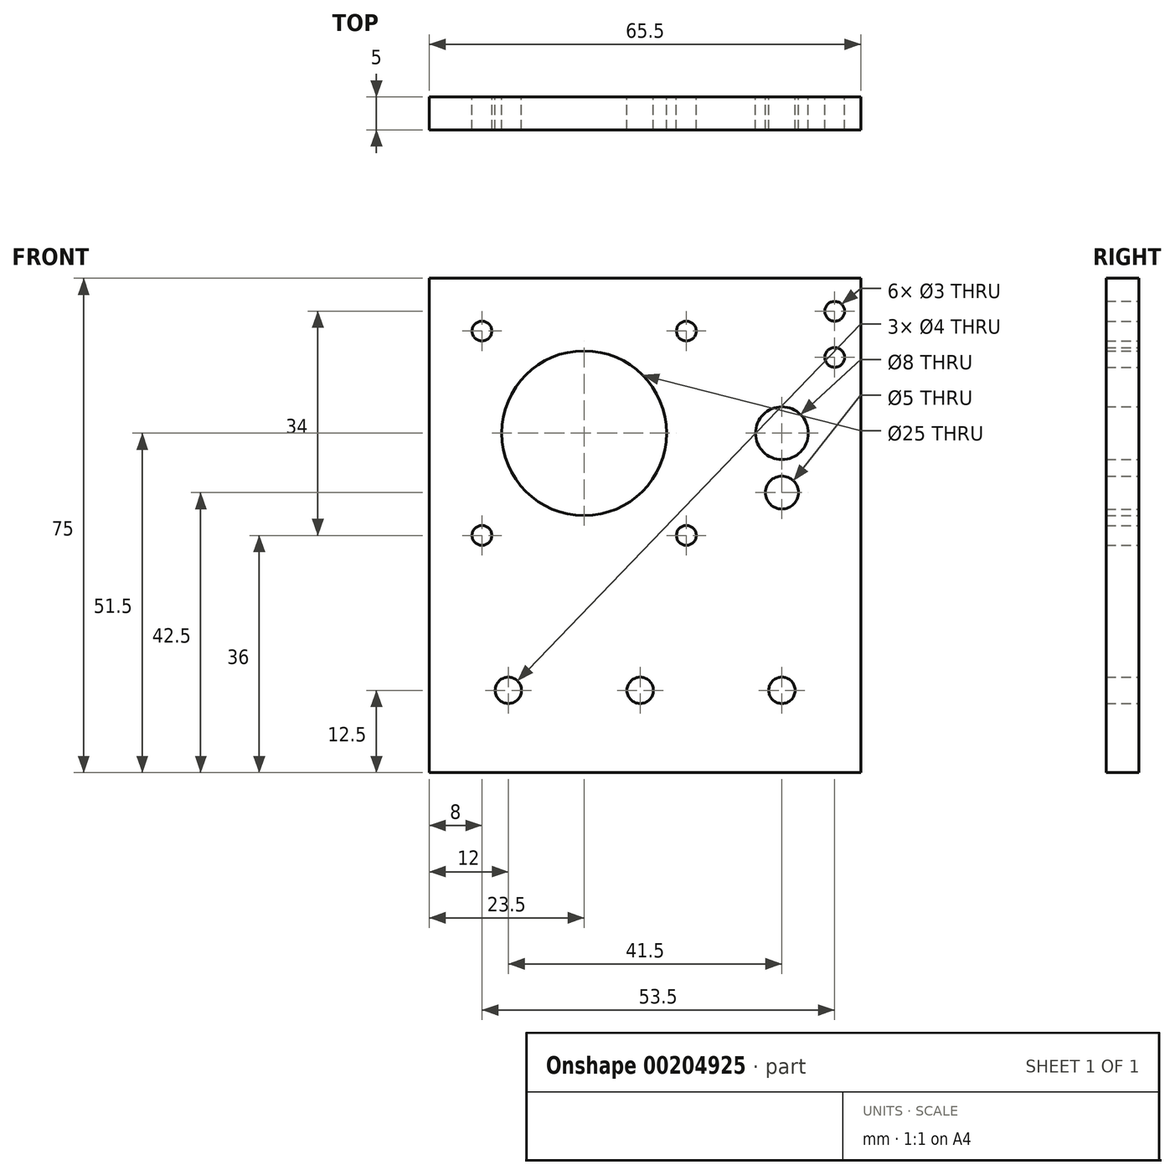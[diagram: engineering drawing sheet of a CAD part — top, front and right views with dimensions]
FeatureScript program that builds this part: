
annotation { "Feature Type Name" : "Feature", "Feature Type Description" : "" }
export const myFeature = defineFeature(function(context is Context, id is Id, definition is map)
    precondition{}
    {
        {
            var Q0;
            Q0=qCreatedBy(makeId("Front.planeOp"),FACE);
            var sketch = newSketch(context, id + "F0", { "sketchPlane" : qUnion([Q0])});
            skLineSegment(sketch, "E0.bottom", {"start": v(0, 0) * mm, "end": v(47, 0) * mm});
            skLineSegment(sketch, "E0.top", {"start": v(0, 50) * mm, "end": v(47, 50) * mm});
            skLineSegment(sketch, "E0.left", {"start": v(0, 0) * mm, "end": v(0, 50) * mm});
            skLineSegment(sketch, "E0.right", {"start": v(47, 0) * mm, "end": v(47, 50) * mm});
            skLineSegment(sketch, "E1.bottom", {"start": v(8, 11) * mm, "end": v(39, 11) * mm, "construction": true});
            skLineSegment(sketch, "E1.top", {"start": v(8, 42) * mm, "end": v(39, 42) * mm, "construction": true});
            skLineSegment(sketch, "E1.left", {"start": v(8, 11) * mm, "end": v(8, 42) * mm, "construction": true});
            skLineSegment(sketch, "E1.right", {"start": v(39, 11) * mm, "end": v(39, 42) * mm, "construction": true});
            skCircle(sketch, "E2", {"center": v(8, 42) * mm, "radius": 1.5 * mm});
            skCircle(sketch, "E3", {"center": v(39, 42) * mm, "radius": 1.5 * mm});
            skCircle(sketch, "E4", {"center": v(39, 11) * mm, "radius": 1.5 * mm});
            skCircle(sketch, "E5", {"center": v(8, 11) * mm, "radius": 1.5 * mm});
            skLineSegment(sketch, "E6", {"start": v(8, 11) * mm, "end": v(39, 42) * mm});
            skPoint(sketch, "E7", {"position": v(23.5, 26.5) * mm});
            skLineSegment(sketch, "E8", {"start": v(23.5, 26.5) * mm, "end": v(53.5, 26.5) * mm, "construction": true});
            skCircle(sketch, "E9", {"center": v(53.5, 26.5) * mm, "radius": 4 * mm});
            skCircle(sketch, "E10", {"center": v(53.5, 26.5) * mm, "radius": 12 * mm, "construction": true});
            skLineSegment(sketch, "E11.top", {"start": v(0, -25) * mm, "end": v(47, -25) * mm});
            skLineSegment(sketch, "E11.left", {"start": v(0, 0) * mm, "end": v(0, -25) * mm});
            skLineSegment(sketch, "E11.right", {"start": v(47, 0) * mm, "end": v(47, -25) * mm});
            skCircle(sketch, "E12", {"center": v(23.5, 26.5) * mm, "radius": 12.5 * mm});
            skLineSegment(sketch, "E13", {"start": v(53.5, 26.5) * mm, "end": v(53.5, 17.5) * mm});
            skCircle(sketch, "E14", {"center": v(53.5, 17.5) * mm, "radius": 2.5 * mm});
            skLineSegment(sketch, "E15", {"start": v(53.5, 26.5) * mm, "end": v(65.5, 26.5) * mm, "construction": true});
            skLineSegment(sketch, "E16", {"start": v(65.5, 26.5) * mm, "end": v(65.5, -25) * mm});
            skLineSegment(sketch, "E17", {"start": v(65.5, -25) * mm, "end": v(47, -25) * mm});
            skLineSegment(sketch, "E18", {"start": v(65.5, 26.5) * mm, "end": v(65.5, 50) * mm});
            skLineSegment(sketch, "E19", {"start": v(65.5, 50) * mm, "end": v(47, 50) * mm});
            skLineSegment(sketch, "E20", {"start": v(47, -12.5) * mm, "end": v(0, -12.5) * mm});
            skLineSegment(sketch, "E21", {"start": v(47, -12.5) * mm, "end": v(65.5, -12.5) * mm});
            skCircle(sketch, "E22", {"center": v(12, -12.5) * mm, "radius": 2 * mm});
            skCircle(sketch, "E23", {"center": v(32, -12.5) * mm, "radius": 2 * mm});
            skCircle(sketch, "E24", {"center": v(53.5, -12.5) * mm, "radius": 2 * mm});
            skLineSegment(sketch, "E25", {"start": v(61.5, 50) * mm, "end": v(61.5, 45) * mm});
            skLineSegment(sketch, "E26", {"start": v(61.5, 45) * mm, "end": v(61.5, 38) * mm});
            skCircle(sketch, "E27", {"center": v(61.5, 45) * mm, "radius": 1.5 * mm});
            skCircle(sketch, "E28", {"center": v(61.5, 38) * mm, "radius": 1.5 * mm});
            skSolve(sketch);
        }
        {
            var Q0;
            {var subQ0=sQuery(id+"F0.wireOp",EDGE,"E0.top");Q0=makeQuery(id+"F0.imprint","IMPRINT",FACE,{"disambiguationData":[TD([[makeQuery(id+"F0.imprint","IMPRINT",EDGE,{"derivedFrom":subQ0}),-1.0]])]});}
            var Q1;
            {var subQ0=sQuery(id+"F0.wireOp",EDGE,"E8");var subQ1=sQuery(id+"F0.wireOp",EDGE,"E0.right");var subQ2=makeQuery(id+"F0.imprint","INTERSECT",VERTEX,{"derivedFrom":[subQ1,subQ0]});Q1=makeQuery(id+"F0.imprint","IMPRINT",FACE,{"disambiguationData":[TD([[makeQuery(id+"F0.imprint","IMPRINT",EDGE,{"disambiguationData":[TD([[subQ2,1.0]])],"derivedFrom":subQ1}),1.0]])]});}
            var Q2;
            {var subQ0=sQuery(id+"F0.wireOp",EDGE,"E8");var subQ1=sQuery(id+"F0.wireOp",EDGE,"E0.right");var subQ2=makeQuery(id+"F0.imprint","INTERSECT",VERTEX,{"derivedFrom":[subQ1,subQ0]});Q2=makeQuery(id+"F0.imprint","IMPRINT",FACE,{"disambiguationData":[TD([[makeQuery(id+"F0.imprint","IMPRINT",EDGE,{"disambiguationData":[TD([[subQ2,-1.0]])],"derivedFrom":subQ1}),1.0]])]});}
            var Q3;
            {var subQ0=sQuery(id+"F0.wireOp",EDGE,"LgC3rz58-ntYh-JOA5-lZNx-mCnSu7RjPkjl");Q3=makeQuery(id+"F0.imprint","IMPRINT",FACE,{"disambiguationData":[TD([[makeQuery(id+"F0.imprint","IMPRINT",EDGE,{"derivedFrom":subQ0}),-1.0]])]});}
            var Q4;
            Q4=makeQuery(id+"F0.imprint","IMPRINT",FACE,{"disambiguationData":[TD([[makeQuery(id+"F0.imprint","IMPRINT",EDGE,{"derivedFrom":sQuery(id+"F0.wireOp",EDGE,"E9")}),-1.0]])]});
            var Q5;
            {var subQ0=sQuery(id+"F0.wireOp",EDGE,"RA9bhjIh-4lE4-AfYF-uRni-oUGcDxIlWYqQ");Q5=makeQuery(id+"F0.imprint","IMPRINT",FACE,{"disambiguationData":[TD([[makeQuery(id+"F0.imprint","IMPRINT",EDGE,{"derivedFrom":subQ0}),-1.0]])]});}
            var Q6;
            Q6=makeQuery(id+"F0.imprint","IMPRINT",FACE,{"disambiguationData":[TD([[makeQuery(id+"F0.imprint","IMPRINT",EDGE,{"derivedFrom":sQuery(id+"F0.wireOp",EDGE,"E0.bottom")}),-1.0]])]});
            var Q7;
            {var subQ5=sQuery(id+"F0.wireOp",EDGE,"E0.right");var subQ7=sQuery(id+"F0.wireOp",EDGE,"E10");var subQ14=makeQuery(id+"F0.imprint","INTERSECT",VERTEX,{"disambiguationData":[OD(0.0)],"derivedFrom":[subQ5,subQ7]});Q7=makeQuery(id+"F0.imprint","IMPRINT",FACE,{"disambiguationData":[TD([[makeQuery(id+"F0.imprint","IMPRINT",EDGE,{"disambiguationData":[TD([[subQ14,-1.0]])],"derivedFrom":subQ5}),-1.0]])]});}
            var Q8;
            {var subQ0=sQuery(id+"F0.wireOp",EDGE,"E10");var subQ1=sQuery(id+"F0.wireOp",EDGE,"E0.right");var subQ2=makeQuery(id+"F0.imprint","INTERSECT",VERTEX,{"disambiguationData":[OD(0.0)],"derivedFrom":[subQ1,subQ0]});Q8=makeQuery(id+"F0.imprint","IMPRINT",FACE,{"disambiguationData":[TD([[makeQuery(id+"F0.imprint","IMPRINT",EDGE,{"disambiguationData":[TD([[subQ2,-1.0]])],"derivedFrom":subQ1}),1.0]])]});}
            var Q9;
            {var subQ5=sQuery(id+"F0.wireOp",EDGE,"E11.top");Q9=makeQuery(id+"F0.imprint","IMPRINT",FACE,{"disambiguationData":[TD([[makeQuery(id+"F0.imprint","IMPRINT",EDGE,{"derivedFrom":subQ5}),1.0]])]});}
            var Q10;
            {var subQ0=sQuery(id+"F0.wireOp",EDGE,"E17");Q10=makeQuery(id+"F0.imprint","IMPRINT",FACE,{"disambiguationData":[TD([[makeQuery(id+"F0.imprint","IMPRINT",EDGE,{"derivedFrom":subQ0}),-1.0]])]});}
            extrude(context, id + "F1", {"entities" : qUnion([Q0, Q1, Q2, Q3, Q4, Q5, Q6, Q7, Q8, Q9, Q10]), "depth" : 5 * mm});
        }
    });
